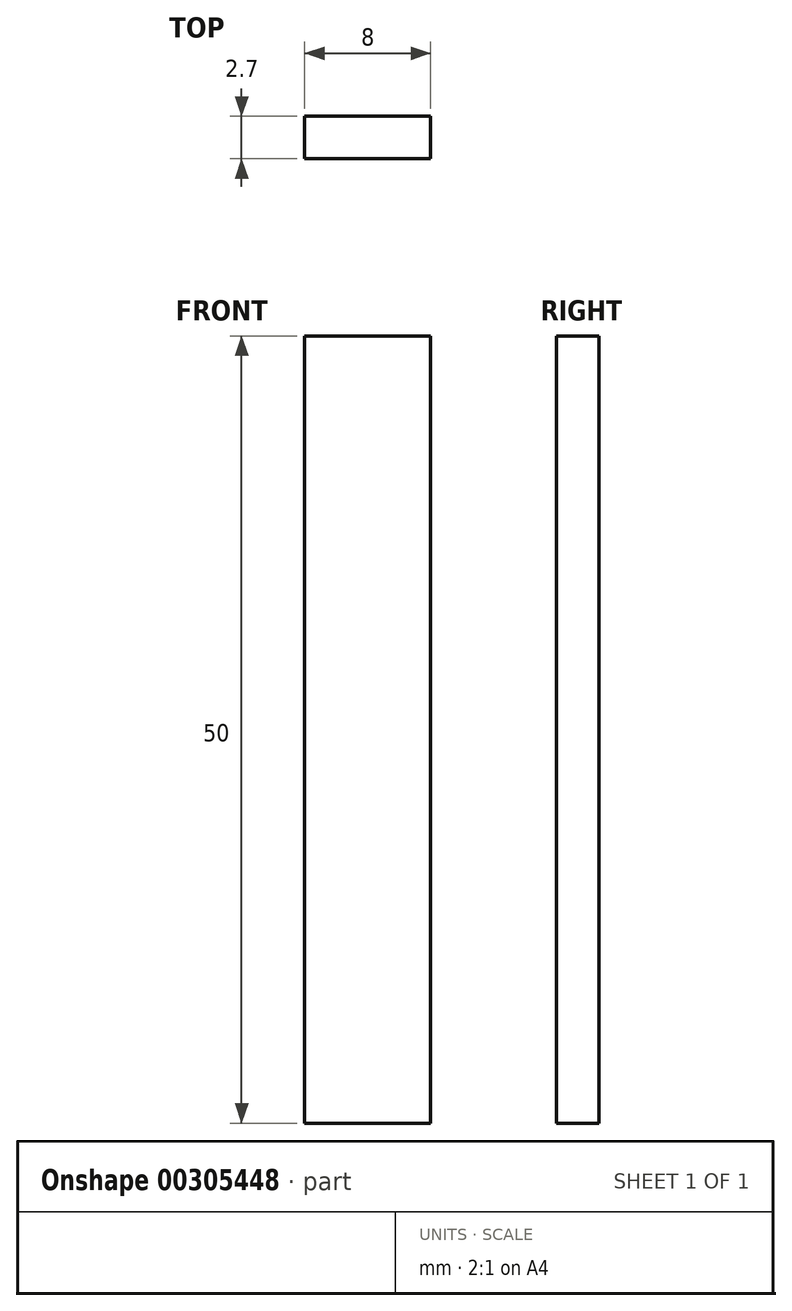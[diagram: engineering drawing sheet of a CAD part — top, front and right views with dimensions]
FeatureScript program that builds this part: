
annotation { "Feature Type Name" : "Feature", "Feature Type Description" : "" }
export const myFeature = defineFeature(function(context is Context, id is Id, definition is map)
    precondition{}
    {
        {
            var Q0;
            Q0=qCreatedBy(makeId("Front.planeOp"),FACE);
            var sketch = newSketch(context, id + "F0", { "sketchPlane" : qUnion([Q0])});
            skLineSegment(sketch, "E0.bottom", {"start": v(-58.3, 45.72) * mm, "end": v(-50.3, 45.72) * mm});
            skLineSegment(sketch, "E0.top", {"start": v(-58.3, -4.28) * mm, "end": v(-50.3, -4.28) * mm});
            skLineSegment(sketch, "E0.left", {"start": v(-58.3, 45.72) * mm, "end": v(-58.3, -4.28) * mm});
            skLineSegment(sketch, "E0.right", {"start": v(-50.3, 45.72) * mm, "end": v(-50.3, -4.28) * mm});
            skSolve(sketch);
        }
        {
            var Q0;
            Q0 = qSketchRegion(id + "F0", true);
            extrude(context, id + "F1", {"entities" : qUnion([Q0]), "depth" : 2.7 * mm});
        }
    });
